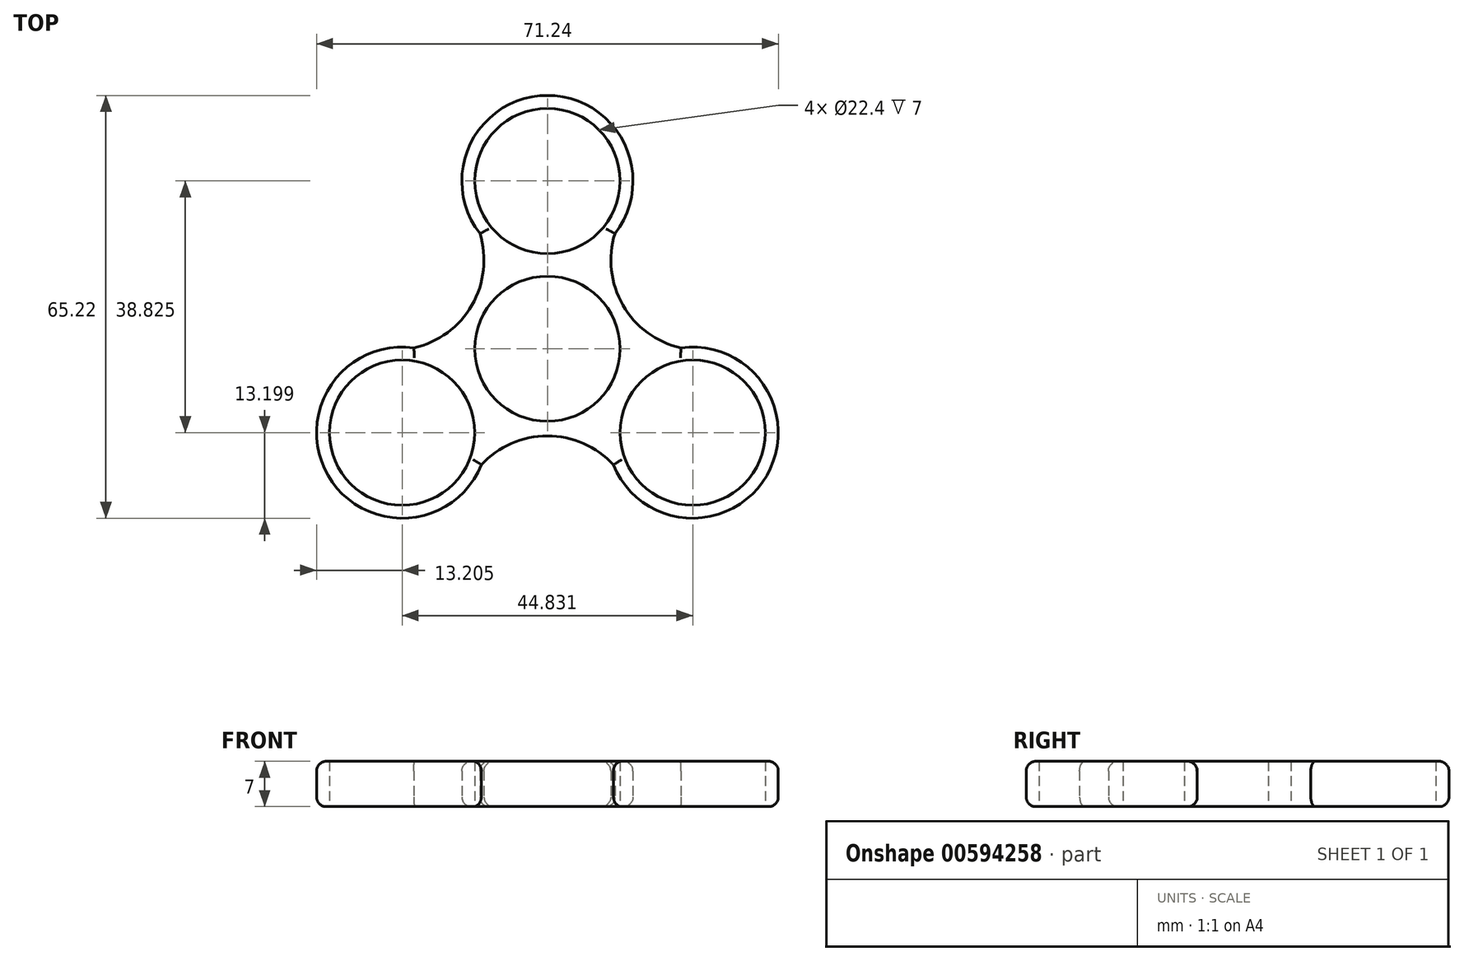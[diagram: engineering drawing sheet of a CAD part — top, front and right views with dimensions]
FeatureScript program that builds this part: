
annotation { "Feature Type Name" : "Feature", "Feature Type Description" : "" }
export const myFeature = defineFeature(function(context is Context, id is Id, definition is map)
    precondition{}
    {
        {
            var Q0;
            Q0=qCreatedBy(makeId("Top.planeOp"),FACE);
            var sketch = newSketch(context, id + "F0", { "sketchPlane" : qUnion([Q0])});
            skCircle(sketch, "E0", {"center": v(0, 0) * mm, "radius": 11.2 * mm});
            skCircle(sketch, "E1", {"center": v(0, 25.88) * mm, "radius": 11.2 * mm});
            skArc(sketch, "E2.1.0", {"start": v(-20.6, 0.13) * mm, "mid": v(-33.85, -19.54) * mm, "end": v(-10.18, -17.9) * mm});
            skCircle(sketch, "E2.1.1", {"center": v(-22.42, -12.94) * mm, "radius": 11.2 * mm});
            skArc(sketch, "E2.2.0", {"start": v(10.18, -17.9) * mm, "mid": v(33.85, -19.54) * mm, "end": v(20.6, 0.13) * mm});
            skCircle(sketch, "E2.2.1", {"center": v(22.42, -12.94) * mm, "radius": 11.2 * mm});
            skArc(sketch, "E3", {"start": v(10.41, 17.77) * mm, "mid": v(11.65, 6.73) * mm, "end": v(20.6, 0.13) * mm});
            skArc(sketch, "E4.1.0", {"start": v(-20.6, 0.13) * mm, "mid": v(-11.65, 6.72) * mm, "end": v(-10.41, 17.77) * mm});
            skArc(sketch, "E4.2.0", {"start": v(10.18, -17.9) * mm, "mid": v(0, -13.45) * mm, "end": v(-10.18, -17.9) * mm});
            skArc(sketch, "E5.trimOffspring", {"start": v(10.41, 17.77) * mm, "mid": v(0, 39.08) * mm, "end": v(-10.41, 17.77) * mm});
            skSolve(sketch);
        }
        {
            var Q0;
            Q0=makeQuery(id+"F0.imprint","IMPRINT",FACE,{"disambiguationData":[TD([[makeQuery(id+"F0.imprint","IMPRINT",EDGE,{"derivedFrom":sQuery(id+"F0.wireOp",EDGE,"E0")}),-1.0]])]});
            extrude(context, id + "F1", {"entities" : qUnion([Q0]), "depth" : 7 * mm, "offsetDistance" : 25 * mm});
        }
        {
            var Q0;
            Q0=makeQuery(id+"F1.opExtrude","CAP_EDGE",EDGE,{"disambiguationData":[OSD([sQuery(id+"F0.wireOp",EDGE,"E4.2.0")])],"isStart":false});
            var Q1;
            Q1=makeQuery(id+"F1.opExtrude","CAP_EDGE",EDGE,{"disambiguationData":[OSD([sQuery(id+"F0.wireOp",EDGE,"E2.1.0")])],"isStart":false});
            var Q2;
            Q2=makeQuery(id+"F1.opExtrude","CAP_EDGE",EDGE,{"disambiguationData":[OSD([sQuery(id+"F0.wireOp",EDGE,"E4.1.0")])],"isStart":false});
            var Q3;
            Q3=makeQuery(id+"F1.opExtrude","CAP_EDGE",EDGE,{"disambiguationData":[OSD([sQuery(id+"F0.wireOp",EDGE,"E5.trimOffspring")])],"isStart":false});
            var Q4;
            Q4=makeQuery(id+"F1.opExtrude","CAP_EDGE",EDGE,{"disambiguationData":[OSD([sQuery(id+"F0.wireOp",EDGE,"E3")])],"isStart":false});
            var Q5;
            Q5=makeQuery(id+"F1.opExtrude","CAP_EDGE",EDGE,{"disambiguationData":[OSD([sQuery(id+"F0.wireOp",EDGE,"E2.2.0")])],"isStart":false});
            fillet(context, id + "F2", {"entities" : qUnion([Q0, Q1, Q2, Q3, Q4, Q5]), "radius" : 1.5 * mm, "tangentPropagation" : true, "allowEdgeOverflow" : false});
        }
        {
            var Q0;
            Q0=makeQuery(id+"F1.opExtrude","CAP_EDGE",EDGE,{"disambiguationData":[OSD([sQuery(id+"F0.wireOp",EDGE,"E2.1.0")])],"isStart":true});
            var Q1;
            Q1=makeQuery(id+"F1.opExtrude","CAP_EDGE",EDGE,{"disambiguationData":[OSD([sQuery(id+"F0.wireOp",EDGE,"E4.2.0")])],"isStart":true});
            var Q2;
            Q2=makeQuery(id+"F1.opExtrude","CAP_EDGE",EDGE,{"disambiguationData":[OSD([sQuery(id+"F0.wireOp",EDGE,"E4.1.0")])],"isStart":true});
            var Q3;
            Q3=makeQuery(id+"F1.opExtrude","CAP_EDGE",EDGE,{"disambiguationData":[OSD([sQuery(id+"F0.wireOp",EDGE,"E5.trimOffspring")])],"isStart":true});
            var Q4;
            Q4=makeQuery(id+"F1.opExtrude","CAP_EDGE",EDGE,{"disambiguationData":[OSD([sQuery(id+"F0.wireOp",EDGE,"E3")])],"isStart":true});
            var Q5;
            Q5=makeQuery(id+"F1.opExtrude","CAP_EDGE",EDGE,{"disambiguationData":[OSD([sQuery(id+"F0.wireOp",EDGE,"E2.2.0")])],"isStart":true});
            fillet(context, id + "F3", {"entities" : qUnion([Q0, Q1, Q2, Q3, Q4, Q5]), "radius" : 1.5 * mm, "tangentPropagation" : true, "allowEdgeOverflow" : false});
        }
    });
